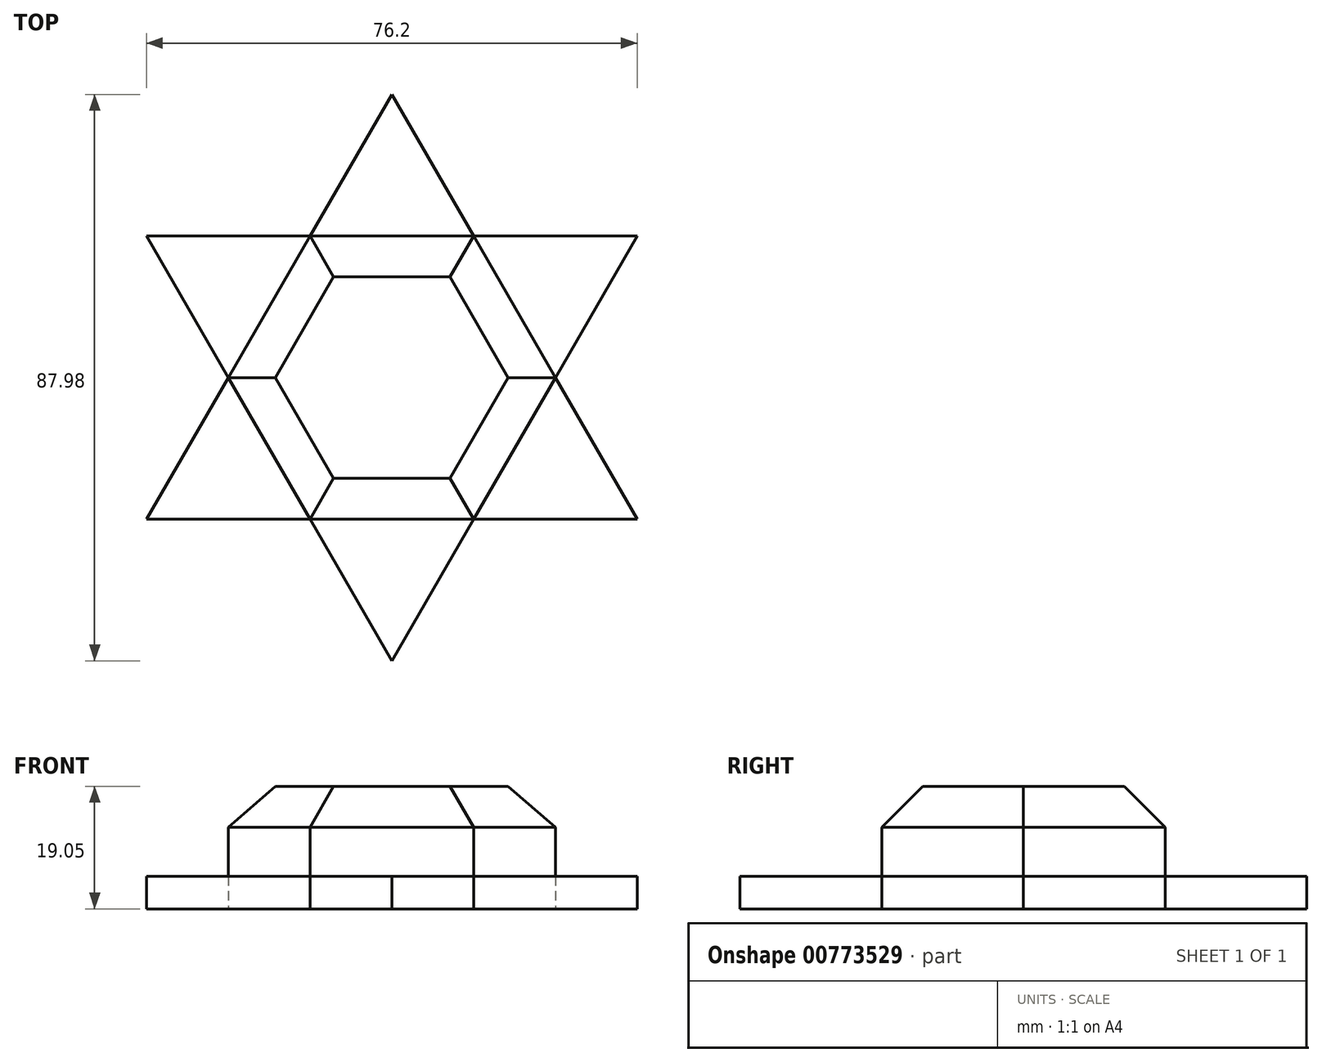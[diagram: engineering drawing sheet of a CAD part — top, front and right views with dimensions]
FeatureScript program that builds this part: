
annotation { "Feature Type Name" : "Feature", "Feature Type Description" : "" }
export const myFeature = defineFeature(function(context is Context, id is Id, definition is map)
    precondition{}
    {
        {
            var Q0;
            Q0=qCreatedBy(makeId("Top.planeOp"),FACE);
            var sketch = newSketch(context, id + "F0", { "sketchPlane" : qUnion([Q0])});
            skCircle(sketch, "E0.cCircle", {"center": v(0, 0) * mm, "radius": 22 * mm, "construction": true});
            skLineSegment(sketch, "E0.0", {"start": v(-38.1, 22) * mm, "end": v(38.1, 22) * mm});
            skLineSegment(sketch, "E0.1", {"start": v(38.1, 22) * mm, "end": v(0, -44) * mm});
            skLineSegment(sketch, "E0.2", {"start": v(0, -44) * mm, "end": v(-38.1, 22) * mm});
            skPoint(sketch, "E0.0.midPoint", {"position": v(0, 22) * mm});
            skLineSegment(sketch, "E1.0", {"start": v(38.1, -22) * mm, "end": v(-38.1, -22) * mm});
            skLineSegment(sketch, "E1.1", {"start": v(-38.1, -22) * mm, "end": v(0, 44) * mm});
            skLineSegment(sketch, "E1.2", {"start": v(0, 44) * mm, "end": v(38.1, -22) * mm});
            skPoint(sketch, "E1.0.midPoint", {"position": v(0, -22) * mm});
            skSolve(sketch);
        }
        {
            var Q0;
            {var subQ5=sQuery(id+"F0.wireOp",EDGE,"E1.1");var subQ9=sQuery(id+"F0.wireOp",EDGE,"E0.0");var subQ10=makeQuery(id+"F0.imprint","INTERSECT",VERTEX,{"derivedFrom":[subQ9,subQ5]});Q0=makeQuery(id+"F0.imprint","IMPRINT",FACE,{"disambiguationData":[TD([[makeQuery(id+"F0.imprint","IMPRINT",EDGE,{"disambiguationData":[TD([[subQ10,-1.0]])],"derivedFrom":subQ9}),-1.0]])]});}
            extrude(context, id + "F1", {"entities" : qUnion([Q0]), "depth" : 19.05 * mm, "offsetDistance" : 25.4 * mm});
        }
        {
            var Q0;
            Q0 = qSketchRegion(id + "F0", true);
            extrude(context, id + "F2", {"entities" : qUnion([Q0]), "operationType" : NewBodyOperationType.ADD, "depth" : 5.08 * mm, "offsetDistance" : 25.4 * mm});
        }
        {
            var Q0;
            Q0=makeQuery(id+"F1.opExtrude","CAP_EDGE",EDGE,{"disambiguationData":[OSD([sQuery(id+"F0.wireOp",EDGE,"E1.0")])],"isStart":false});
            var Q1;
            Q1=makeQuery(id+"F1.opExtrude","CAP_EDGE",EDGE,{"disambiguationData":[OSD([sQuery(id+"F0.wireOp",EDGE,"E0.1")])],"isStart":false});
            var Q2;
            Q2=makeQuery(id+"F1.opExtrude","CAP_EDGE",EDGE,{"disambiguationData":[OSD([sQuery(id+"F0.wireOp",EDGE,"E1.2")])],"isStart":false});
            var Q3;
            Q3=makeQuery(id+"F1.opExtrude","CAP_EDGE",EDGE,{"disambiguationData":[OSD([sQuery(id+"F0.wireOp",EDGE,"E0.0")])],"isStart":false});
            var Q4;
            Q4=makeQuery(id+"F1.opExtrude","CAP_EDGE",EDGE,{"disambiguationData":[OSD([sQuery(id+"F0.wireOp",EDGE,"E1.1")])],"isStart":false});
            var Q5;
            Q5=makeQuery(id+"F1.opExtrude","CAP_EDGE",EDGE,{"disambiguationData":[OSD([sQuery(id+"F0.wireOp",EDGE,"E0.2")])],"isStart":false});
            chamfer(context, id + "F3", {"entities" : qUnion([Q0, Q1, Q2, Q3, Q4, Q5]), "width" : 6.35 * mm, "tangentPropagation" : true});
        }
    });
